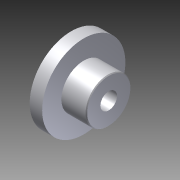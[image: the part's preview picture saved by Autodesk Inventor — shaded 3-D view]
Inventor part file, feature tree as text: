
AUTODESK INVENTOR PART (.ipt)
format: ipt  version: 2012 (Build 160160000, 160)  size: 601,088 bytes
history: native  units: in
note: dims shown in document units (in); Inventor stores cm internally (conversion verified against a paired STEP export)
features: extrude x2, sketch x1, imported_body x1
ambient origin geometry x8: Origin, YZ Plane, XZ Plane, XY Plane, X Axis, Y Axis, Z Axis, Center Point
feature tree (4):
  sketch  "Sketch1"  dims[d0=0.25in d1=0.5625in d2=0.0in d3=1.25in d4=1.0in d5=0.0in]
  extrude  "Extrusion1"  Depth=0.5625in TaperAngle=0.0deg
  extrude  "Extrusion2"  Depth=1.25in
  imported_body  "Base1"
